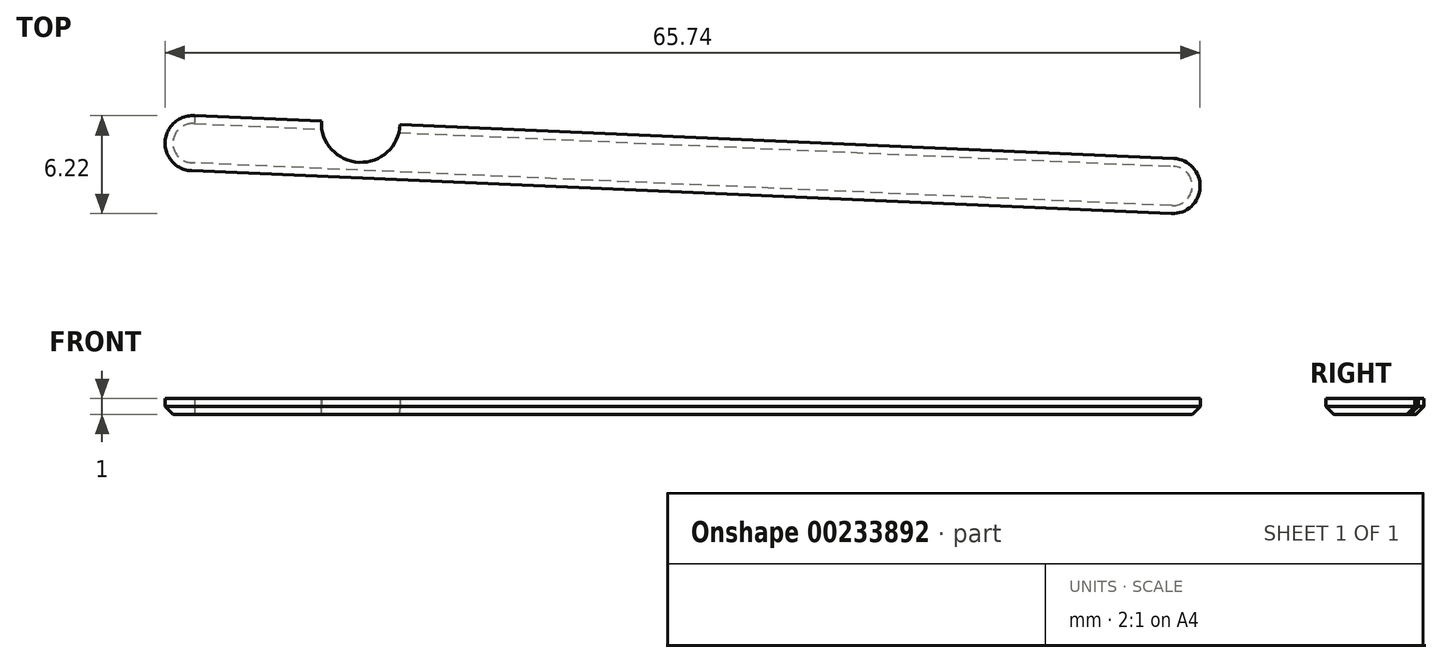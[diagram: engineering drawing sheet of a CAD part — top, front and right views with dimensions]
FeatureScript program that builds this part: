
annotation { "Feature Type Name" : "Feature", "Feature Type Description" : "" }
export const myFeature = defineFeature(function(context is Context, id is Id, definition is map)
    precondition{}
    {
        {
            var Q0;
            Q0=qCreatedBy(makeId("Top.planeOp"),FACE);
            var sketch = newSketch(context, id + "F0", { "sketchPlane" : qUnion([Q0])});
            skCircle(sketch, "E0", {"center": v(-1.57, 0) * mm, "radius": 1.75 * mm});
            skCircle(sketch, "E1", {"center": v(60.67, -2.72) * mm, "radius": 1.75 * mm});
            skLineSegment(sketch, "E2", {"start": v(-1.43, 1.74) * mm, "end": v(60.75, -0.97) * mm});
            skLineSegment(sketch, "E3", {"start": v(-1.64, -1.75) * mm, "end": v(60.6, -4.47) * mm});
            skCircle(sketch, "E4", {"center": v(9.1, 1.28) * mm, "radius": 2.5 * mm});
            skSolve(sketch);
        }
        {
            var Q0;
            {var subQ8=sQuery(id+"F0.wireOp",EDGE,"E3");Q0=makeQuery(id+"F0.imprint","IMPRINT",FACE,{"disambiguationData":[TD([[makeQuery(id+"F0.imprint","IMPRINT",EDGE,{"derivedFrom":subQ8}),1.0]])]});}
            var Q1;
            {var subQ0=sQuery(id+"F0.wireOp",EDGE,"E0");var subQ1=makeQuery(id+"F0.imprint","INTERSECT",VERTEX,{"derivedFrom":[subQ0,sQuery(id+"F0.wireOp",EDGE,"E2")]});Q1=makeQuery(id+"F0.imprint","IMPRINT",FACE,{"disambiguationData":[TD([[makeQuery(id+"F0.imprint","IMPRINT",EDGE,{"disambiguationData":[TD([[subQ1,-1.0]])],"derivedFrom":subQ0}),1.0]])]});}
            var Q2;
            {var subQ0=sQuery(id+"F0.wireOp",EDGE,"E1");var subQ1=makeQuery(id+"F0.imprint","INTERSECT",VERTEX,{"derivedFrom":[subQ0,sQuery(id+"F0.wireOp",EDGE,"E2")]});Q2=makeQuery(id+"F0.imprint","IMPRINT",FACE,{"disambiguationData":[TD([[makeQuery(id+"F0.imprint","IMPRINT",EDGE,{"disambiguationData":[TD([[subQ1,-1.0]])],"derivedFrom":subQ0}),1.0]])]});}
            extrude(context, id + "F1", {"entities" : qUnion([Q0, Q1, Q2]), "depth" : 1 * mm});
        }
        {
            var Q0;
            Q0=makeQuery(id+"F1.opExtrude","CAP_EDGE",EDGE,{"disambiguationData":[OSD([sQuery(id+"F0.wireOp",EDGE,"E3")])],"isStart":true});
            chamfer(context, id + "F2", {"entities" : qUnion([Q0]), "width" : 0.5 * mm, "tangentPropagation" : true});
        }
    });
